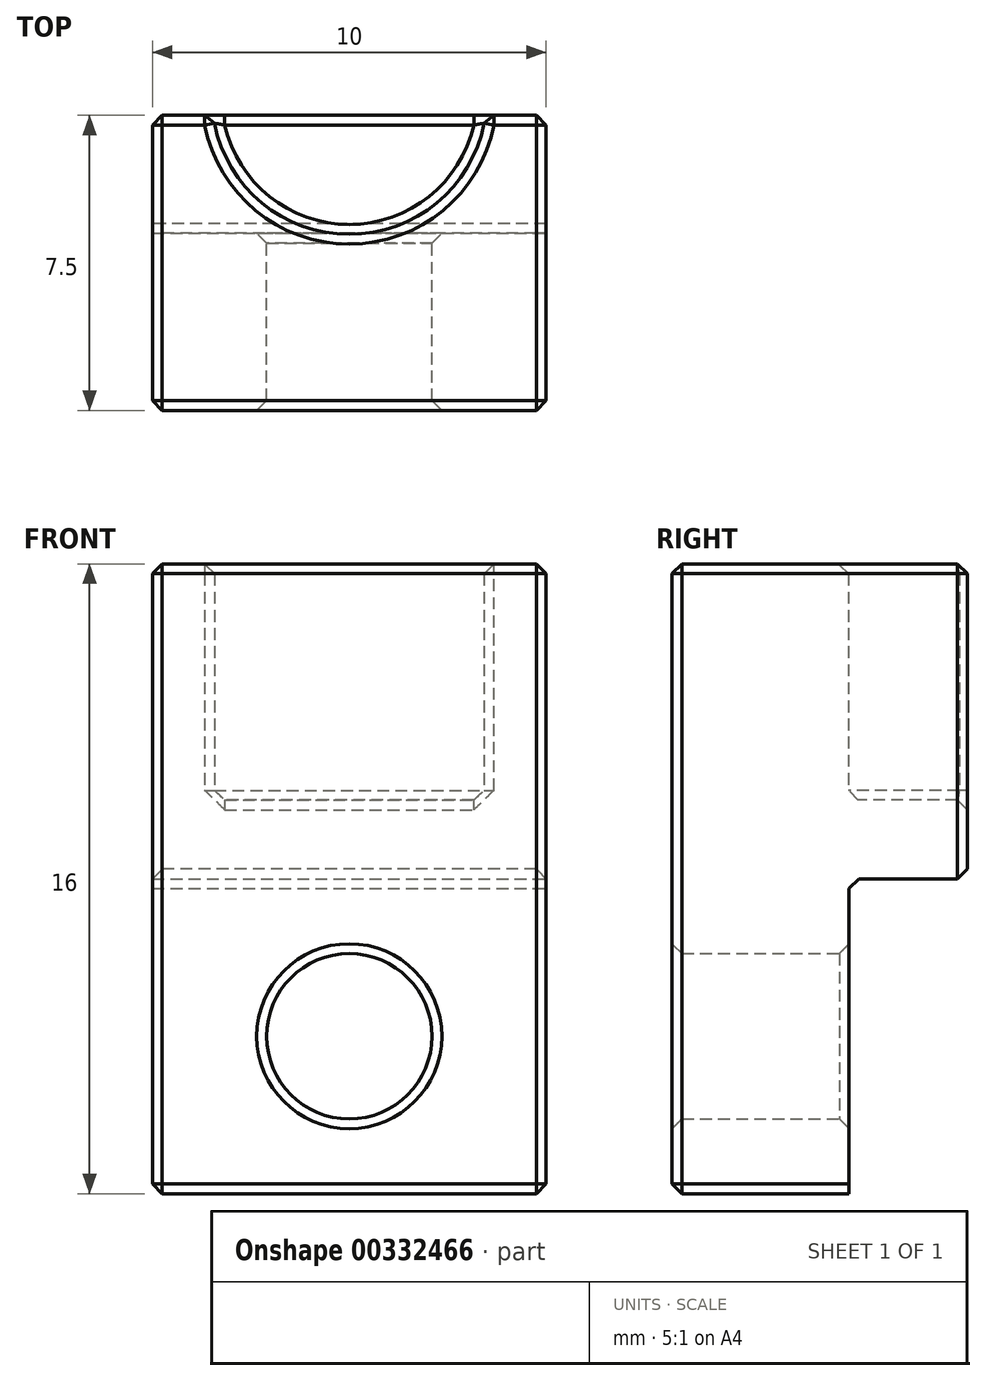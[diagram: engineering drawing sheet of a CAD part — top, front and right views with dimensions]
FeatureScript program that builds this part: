
annotation { "Feature Type Name" : "Feature", "Feature Type Description" : "" }
export const myFeature = defineFeature(function(context is Context, id is Id, definition is map)
    precondition{}
    {
        {
            var Q0;
            Q0=qCreatedBy(makeId("Top.planeOp"),FACE);
            var sketch = newSketch(context, id + "F0", { "sketchPlane" : qUnion([Q0])});
            skLineSegment(sketch, "E0.bottom", {"start": v(0, -9.52) * mm, "end": v(0, -9.52) * mm});
            skLineSegment(sketch, "E0.top", {"start": v(0, 9.52) * mm, "end": v(0, 9.52) * mm});
            skLineSegment(sketch, "E0.left", {"start": v(3.5, -6.03) * mm, "end": v(3.5, 6.03) * mm});
            skLineSegment(sketch, "E0.right", {"start": v(-3.5, -6.03) * mm, "end": v(-3.5, 6.03) * mm});
            skPoint(sketch, "E0.middle", {"position": v(0, 0) * mm});
            skPoint(sketch, "E1.visualSharp", {"position": v(-3.5, 9.52) * mm});
            skArc(sketch, "E1.filletArc", {"start": v(0, 9.52) * mm, "mid": v(-2.47, 8.5) * mm, "end": v(-3.5, 6.03) * mm});
            skPoint(sketch, "E2.visualSharp", {"position": v(3.5, 9.52) * mm});
            skArc(sketch, "E2.filletArc", {"start": v(3.5, 6.03) * mm, "mid": v(2.47, 8.5) * mm, "end": v(0, 9.52) * mm});
            skPoint(sketch, "E3.visualSharp", {"position": v(3.5, -9.52) * mm});
            skArc(sketch, "E3.filletArc", {"start": v(0, -9.52) * mm, "mid": v(2.47, -8.5) * mm, "end": v(3.5, -6.03) * mm});
            skPoint(sketch, "E4.visualSharp", {"position": v(-3.5, -9.53) * mm});
            skArc(sketch, "E4.filletArc", {"start": v(-3.5, -6.03) * mm, "mid": v(-2.47, -8.5) * mm, "end": v(0, -9.52) * mm});
            skSolve(sketch);
        }
        {
            var Q0;
            Q0=makeQuery(id+"F0.imprint","IMPRINT",FACE,{"disambiguationData":[TD([[makeQuery(id+"F0.imprint","IMPRINT",EDGE,{"derivedFrom":sQuery(id+"F0.wireOp",EDGE,"E0.left")}),1.0]])]});
            extrude(context, id + "F1", {"entities" : qUnion([Q0]), "depth" : 7.62 * mm});
        }
        {
            var Q0;
            Q0=qCreatedBy(makeId("Top.planeOp"),FACE);
            var sketch = newSketch(context, id + "F2", { "sketchPlane" : qUnion([Q0])});
            skLineSegment(sketch, "E5.bottom", {"start": v(5, -9.5) * mm, "end": v(-5, -9.5) * mm});
            skLineSegment(sketch, "E5.top", {"start": v(5, 9.5) * mm, "end": v(-5, 9.5) * mm});
            skLineSegment(sketch, "E5.left", {"start": v(5, -9.5) * mm, "end": v(5, 9.5) * mm});
            skLineSegment(sketch, "E5.right", {"start": v(-5, -9.5) * mm, "end": v(-5, 9.5) * mm});
            skPoint(sketch, "E5.middle", {"position": v(0, 0) * mm});
            skSolve(sketch);
        }
        {
            var Q0;
            Q0 = qSketchRegion(id + "F2", true);
            extrude(context, id + "F3", {"entities" : qUnion([Q0]), "oppositeDirection" : true, "depth" : 10 * mm, "hasSecondDirection" : true, "secondDirectionOppositeDirection" : false, "secondDirectionDepth" : -2 * mm});
        }
        {
            var Q0;
            Q0=makeQuery(id+"F3.opExtrude","SWEPT_FACE",FACE,{"disambiguationData":[OSD([sQuery(id+"F2.wireOp",EDGE,"E5.top")])]});
            var sketch = newSketch(context, id + "F4", { "sketchPlane" : qUnion([Q0])});
            skPoint(sketch, "E6", {"position": v(0, -6) * mm});
            skPoint(sketch, "E6.positionSnap0", {"position": v(-5, -6) * mm});
            skPoint(sketch, "E6.positionSnap1", {"position": v(0, -2) * mm});
            skSolve(sketch);
        }
        {
            var Q0;
            Q0=sQuery(id+"F4.wireOp",VERTEX,"E6");
            var Q1;
            Q1=makeQuery(id+"F3.opExtrude","SWEPT_BODY",BODY,{"disambiguationData":[OSD([sQuery(id+"F2.wireOp",EDGE,"E5.bottom"),sQuery(id+"F2.wireOp",EDGE,"E5.top"),sQuery(id+"F2.wireOp",EDGE,"E5.left"),sQuery(id+"F2.wireOp",EDGE,"E5.right")])]});
            hole(context, id + "F5", {"style" : HoleStyle.SIMPLE, "endStyle" : HoleEndStyle.THROUGH, "standardTappedOrClearance" : lookupTablePath({ "standard" : "ISO", "engagement" : "75%", "pitch" : "0.75 mm", "size" : "M4", "type" : "Tapped" }), "standardBlindInLast" : lookupTablePath({ "standard" : "ISO", "engagement" : "75%", "pitch" : "0.75 mm", "size" : "M4", "type" : "Tapped" }), "holeDiameter" : 3.2 * mm, "showTappedDepth" : true, "tappedDepth" : 12 * mm, "tapClearance" : 3, "startFromSketch" : true, "locations" : qUnion([Q0]), "scope" : qUnion([Q1])});
        }
        {
            var Q0;
            Q0=qCreatedBy(makeId("Front.planeOp"),FACE);
            var sketch = newSketch(context, id + "F6", { "sketchPlane" : qUnion([Q0])});
            skLineSegment(sketch, "E7.0", {"start": v(5, -10) * mm, "end": v(-5, -10) * mm});
            skCircle(sketch, "E7.2", {"center": v(0, -6) * mm, "radius": 2.1 * mm});
            skLineSegment(sketch, "E7.3", {"start": v(-5, -10) * mm, "end": v(-5, -2) * mm});
            skLineSegment(sketch, "E7.4", {"start": v(5, -10) * mm, "end": v(5, -2) * mm});
            skLineSegment(sketch, "E8.top", {"start": v(5, 6) * mm, "end": v(-5, 6) * mm});
            skLineSegment(sketch, "E8.left", {"start": v(5, -10) * mm, "end": v(5, 6) * mm});
            skLineSegment(sketch, "E8.right", {"start": v(-5, -10) * mm, "end": v(-5, 6) * mm});
            skPoint(sketch, "E8.middle", {"position": v(0, -2) * mm});
            skSolve(sketch);
        }
        {
            var Q0;
            Q0 = qSketchRegion(id + "F6", true);
            extrude(context, id + "F7", {"entities" : qUnion([Q0]), "depth" : 14 * mm, "hasSecondDirection" : true, "secondDirectionOppositeDirection" : false, "secondDirectionDepth" : 6.5 * mm});
        }
        {
            var Q0;
            Q0=makeQuery(id+"F1.opExtrude","SWEPT_BODY",BODY,{"disambiguationData":[OSD([sQuery(id+"F0.wireOp",EDGE,"E0.left"),sQuery(id+"F0.wireOp",EDGE,"E0.right"),sQuery(id+"F0.wireOp",EDGE,"E1.filletArc"),sQuery(id+"F0.wireOp",EDGE,"E2.filletArc"),sQuery(id+"F0.wireOp",EDGE,"E3.filletArc"),sQuery(id+"F0.wireOp",EDGE,"E4.filletArc")])]});
            var Q1;
            Q1=makeQuery(id+"F3.opExtrude","SWEPT_BODY",BODY,{"disambiguationData":[OSD([sQuery(id+"F2.wireOp",EDGE,"E5.bottom"),sQuery(id+"F2.wireOp",EDGE,"E5.top"),sQuery(id+"F2.wireOp",EDGE,"E5.left"),sQuery(id+"F2.wireOp",EDGE,"E5.right")])]});
            var Q2;
            Q2=makeQuery(id+"F7.opExtrude","SWEPT_BODY",BODY,{"disambiguationData":[OSD([sQuery(id+"F6.wireOp",EDGE,"E7.2"),sQuery(id+"F6.wireOp",EDGE,"E7.0"),sQuery(id+"F6.wireOp",EDGE,"E8.top"),sQuery(id+"F6.wireOp",EDGE,"E8.left"),sQuery(id+"F6.wireOp",EDGE,"E8.right")])]});
            booleanBodies(context, id + "F8", {"operationType" : BooleanOperationType.SUBTRACTION, "tools" : qUnion([Q0, Q1]), "targets" : qUnion([Q2])});
        }
        {
            var Q0;
            Q0=makeQuery(id+"F8.opBoolean","COPY",EDGE,{"derivedFrom":makeQuery(id+"F1.opExtrude","CAP_EDGE",EDGE,{"disambiguationData":[OSD([sQuery(id+"F0.wireOp",EDGE,"E3.filletArc"),sQuery(id+"F0.wireOp",EDGE,"E4.filletArc")])],"isStart":true})});
            var Q1;
            Q1=makeQuery(id+"F8.opBoolean","COPY",EDGE,{"derivedFrom":makeQuery(id+"F3.opExtrude","CAP_EDGE",EDGE,{"disambiguationData":[OSD([sQuery(id+"F2.wireOp",EDGE,"E5.bottom")])],"isStart":false})});
            var Q2;
            Q2=makeQuery(id+"F8.opBoolean","INTERSECT",EDGE,{"derivedFrom":[makeQuery(id+"F3.opExtrude","CAP_FACE",FACE,{"disambiguationData":[OSD([sQuery(id+"F2.wireOp",EDGE,"E5.bottom"),sQuery(id+"F2.wireOp",EDGE,"E5.top"),sQuery(id+"F2.wireOp",EDGE,"E5.left"),sQuery(id+"F2.wireOp",EDGE,"E5.right")])],"isStart":true}),makeQuery(id+"F7.opExtrude","CAP_FACE",FACE,{"disambiguationData":[OSD([sQuery(id+"F6.wireOp",EDGE,"E7.2"),sQuery(id+"F6.wireOp",EDGE,"E7.0"),sQuery(id+"F6.wireOp",EDGE,"E8.top"),sQuery(id+"F6.wireOp",EDGE,"E8.left"),sQuery(id+"F6.wireOp",EDGE,"E8.right")])],"isStart":true})]});
            var Q3;
            Q3=makeQuery(id+"F8.opBoolean","INTERSECT",EDGE,{"derivedFrom":[makeQuery(id+"F1.opExtrude","SWEPT_FACE",FACE,{"disambiguationData":[OSD([sQuery(id+"F0.wireOp",EDGE,"E3.filletArc"),sQuery(id+"F0.wireOp",EDGE,"E4.filletArc")])]}),makeQuery(id+"F7.opExtrude","SWEPT_FACE",FACE,{"disambiguationData":[OSD([sQuery(id+"F6.wireOp",EDGE,"E8.top")])]})]});
            var Q4;
            Q4=makeQuery(id+"F8.opBoolean","COPY",EDGE,{"derivedFrom":makeQuery(id+"F3.opExtrude","SWEPT_EDGE",EDGE,{"disambiguationData":[OSD([sQuery(id+"F2.wireOp",EDGE,"E5.bottom"),sQuery(id+"F2.wireOp",EDGE,"E5.right")])]})});
            var Q5;
            Q5=makeQuery(id+"F7.opExtrude","CAP_EDGE",EDGE,{"disambiguationData":[OSD([sQuery(id+"F6.wireOp",EDGE,"E8.top")])],"isStart":false});
            var Q6;
            Q6=makeQuery(id+"F7.opExtrude","CAP_EDGE",EDGE,{"disambiguationData":[OSD([sQuery(id+"F6.wireOp",EDGE,"E8.right")])],"isStart":true});
            var Q7;
            Q7=makeQuery(id+"F8.opBoolean","INTERSECT",EDGE,{"derivedFrom":[makeQuery(id+"F3.opExtrude","SWEPT_FACE",FACE,{"disambiguationData":[OSD([sQuery(id+"F2.wireOp",EDGE,"E5.bottom")])]}),makeQuery(id+"F7.opExtrude","SWEPT_FACE",FACE,{"disambiguationData":[OSD([sQuery(id+"F6.wireOp",EDGE,"E7.2")])]})]});
            var Q8;
            Q8=makeQuery(id+"F8.opBoolean","INTERSECT",EDGE,{"derivedFrom":[makeQuery(id+"F1.opExtrude","CAP_FACE",FACE,{"disambiguationData":[OSD([sQuery(id+"F0.wireOp",EDGE,"E0.left"),sQuery(id+"F0.wireOp",EDGE,"E0.right"),sQuery(id+"F0.wireOp",EDGE,"E1.filletArc"),sQuery(id+"F0.wireOp",EDGE,"E2.filletArc"),sQuery(id+"F0.wireOp",EDGE,"E3.filletArc"),sQuery(id+"F0.wireOp",EDGE,"E4.filletArc")])],"isStart":true}),makeQuery(id+"F7.opExtrude","CAP_FACE",FACE,{"disambiguationData":[OSD([sQuery(id+"F6.wireOp",EDGE,"E7.2"),sQuery(id+"F6.wireOp",EDGE,"E7.0"),sQuery(id+"F6.wireOp",EDGE,"E8.top"),sQuery(id+"F6.wireOp",EDGE,"E8.left"),sQuery(id+"F6.wireOp",EDGE,"E8.right")])],"isStart":true})]});
            var Q9;
            Q9=makeQuery(id+"F8.opBoolean","INTERSECT",EDGE,{"disambiguationData":[OD(1.0)],"derivedFrom":[makeQuery(id+"F1.opExtrude","SWEPT_FACE",FACE,{"disambiguationData":[OSD([sQuery(id+"F0.wireOp",EDGE,"E3.filletArc"),sQuery(id+"F0.wireOp",EDGE,"E4.filletArc")])]}),makeQuery(id+"F7.opExtrude","CAP_FACE",FACE,{"disambiguationData":[OSD([sQuery(id+"F6.wireOp",EDGE,"E7.2"),sQuery(id+"F6.wireOp",EDGE,"E7.0"),sQuery(id+"F6.wireOp",EDGE,"E8.top"),sQuery(id+"F6.wireOp",EDGE,"E8.left"),sQuery(id+"F6.wireOp",EDGE,"E8.right")])],"isStart":true})]});
            var Q10;
            Q10=makeQuery(id+"F7.opExtrude","SWEPT_EDGE",EDGE,{"disambiguationData":[OSD([sQuery(id+"F6.wireOp",EDGE,"E8.top"),sQuery(id+"F6.wireOp",EDGE,"E8.right")])]});
            var Q11;
            Q11=makeQuery(id+"F7.opExtrude","SWEPT_EDGE",EDGE,{"disambiguationData":[OSD([sQuery(id+"F6.wireOp",EDGE,"E8.top"),sQuery(id+"F6.wireOp",EDGE,"E8.left")])]});
            var Q12;
            Q12=makeQuery(id+"F7.opExtrude","CAP_EDGE",EDGE,{"disambiguationData":[OSD([sQuery(id+"F6.wireOp",EDGE,"E8.right")])],"isStart":false});
            var Q13;
            Q13=makeQuery(id+"F8.opBoolean","COPY",EDGE,{"derivedFrom":makeQuery(id+"F3.opExtrude","SWEPT_EDGE",EDGE,{"disambiguationData":[OSD([sQuery(id+"F2.wireOp",EDGE,"E5.bottom"),sQuery(id+"F2.wireOp",EDGE,"E5.left")])]})});
            var Q14;
            {var subQ0=sQuery(id+"F6.wireOp",EDGE,"E8.left");var subQ1=sQuery(id+"F6.wireOp",EDGE,"E8.top");Q14=makeQuery(id+"F8.opBoolean","SPLIT",EDGE,{"disambiguationData":[TD([makeQuery(id+"F7.opExtrude","SWEPT_FACE",FACE,{"disambiguationData":[OSD([subQ0])]})])],"derivedFrom":makeQuery(id+"F7.opExtrude","CAP_EDGE",EDGE,{"disambiguationData":[OSD([subQ1])],"isStart":true})});}
            var Q15;
            Q15=makeQuery(id+"F8.opBoolean","COPY",EDGE,{"derivedFrom":makeQuery(id+"F3.opExtrude","CAP_EDGE",EDGE,{"disambiguationData":[OSD([sQuery(id+"F2.wireOp",EDGE,"E5.bottom")])],"isStart":true})});
            var Q16;
            Q16=makeQuery(id+"F8.opBoolean","COPY",EDGE,{"derivedFrom":makeQuery(id+"F3.opExtrude","CAP_EDGE",EDGE,{"disambiguationData":[OSD([sQuery(id+"F2.wireOp",EDGE,"E5.left")])],"isStart":true})});
            var Q17;
            Q17=makeQuery(id+"F8.opBoolean","COPY",EDGE,{"derivedFrom":makeQuery(id+"F3.opExtrude","CAP_EDGE",EDGE,{"disambiguationData":[OSD([sQuery(id+"F2.wireOp",EDGE,"E5.right")])],"isStart":true})});
            var Q18;
            Q18=makeQuery(id+"F7.opExtrude","SWEPT_EDGE",EDGE,{"disambiguationData":[OSD([sQuery(id+"F6.wireOp",EDGE,"E7.0"),sQuery(id+"F6.wireOp",EDGE,"E8.left")])]});
            var Q19;
            Q19=makeQuery(id+"F7.opExtrude","SWEPT_EDGE",EDGE,{"disambiguationData":[OSD([sQuery(id+"F6.wireOp",EDGE,"E7.0"),sQuery(id+"F6.wireOp",EDGE,"E8.right")])]});
            var Q20;
            Q20=makeQuery(id+"F7.opExtrude","CAP_EDGE",EDGE,{"disambiguationData":[OSD([sQuery(id+"F6.wireOp",EDGE,"E8.left")])],"isStart":true});
            var Q21;
            Q21=makeQuery(id+"F7.opExtrude","CAP_EDGE",EDGE,{"disambiguationData":[OSD([sQuery(id+"F6.wireOp",EDGE,"E8.left")])],"isStart":false});
            var Q22;
            Q22=makeQuery(id+"F7.opExtrude","CAP_EDGE",EDGE,{"disambiguationData":[OSD([sQuery(id+"F6.wireOp",EDGE,"E7.0")])],"isStart":false});
            var Q23;
            Q23=makeQuery(id+"F7.opExtrude","CAP_EDGE",EDGE,{"disambiguationData":[OSD([sQuery(id+"F6.wireOp",EDGE,"E7.2")])],"isStart":false});
            var Q24;
            {var subQ0=sQuery(id+"F6.wireOp",EDGE,"E8.right");var subQ1=sQuery(id+"F6.wireOp",EDGE,"E8.top");Q24=makeQuery(id+"F8.opBoolean","SPLIT",EDGE,{"disambiguationData":[TD([makeQuery(id+"F7.opExtrude","SWEPT_FACE",FACE,{"disambiguationData":[OSD([subQ0])]})])],"derivedFrom":makeQuery(id+"F7.opExtrude","CAP_EDGE",EDGE,{"disambiguationData":[OSD([subQ1])],"isStart":true})});}
            var Q25;
            Q25=makeQuery(id+"F8.opBoolean","INTERSECT",EDGE,{"disambiguationData":[OD(0.0)],"derivedFrom":[makeQuery(id+"F1.opExtrude","SWEPT_FACE",FACE,{"disambiguationData":[OSD([sQuery(id+"F0.wireOp",EDGE,"E3.filletArc"),sQuery(id+"F0.wireOp",EDGE,"E4.filletArc")])]}),makeQuery(id+"F7.opExtrude","CAP_FACE",FACE,{"disambiguationData":[OSD([sQuery(id+"F6.wireOp",EDGE,"E7.2"),sQuery(id+"F6.wireOp",EDGE,"E7.0"),sQuery(id+"F6.wireOp",EDGE,"E8.top"),sQuery(id+"F6.wireOp",EDGE,"E8.left"),sQuery(id+"F6.wireOp",EDGE,"E8.right")])],"isStart":true})]});
            chamfer(context, id + "F9", {"entities" : qUnion([Q0, Q1, Q2, Q3, Q4, Q5, Q6, Q7, Q8, Q9, Q10, Q11, Q12, Q13, Q14, Q15, Q16, Q17, Q18, Q19, Q20, Q21, Q22, Q23, Q24, Q25]), "width" : .25 * mm, "tangentPropagation" : true});
        }
    });
